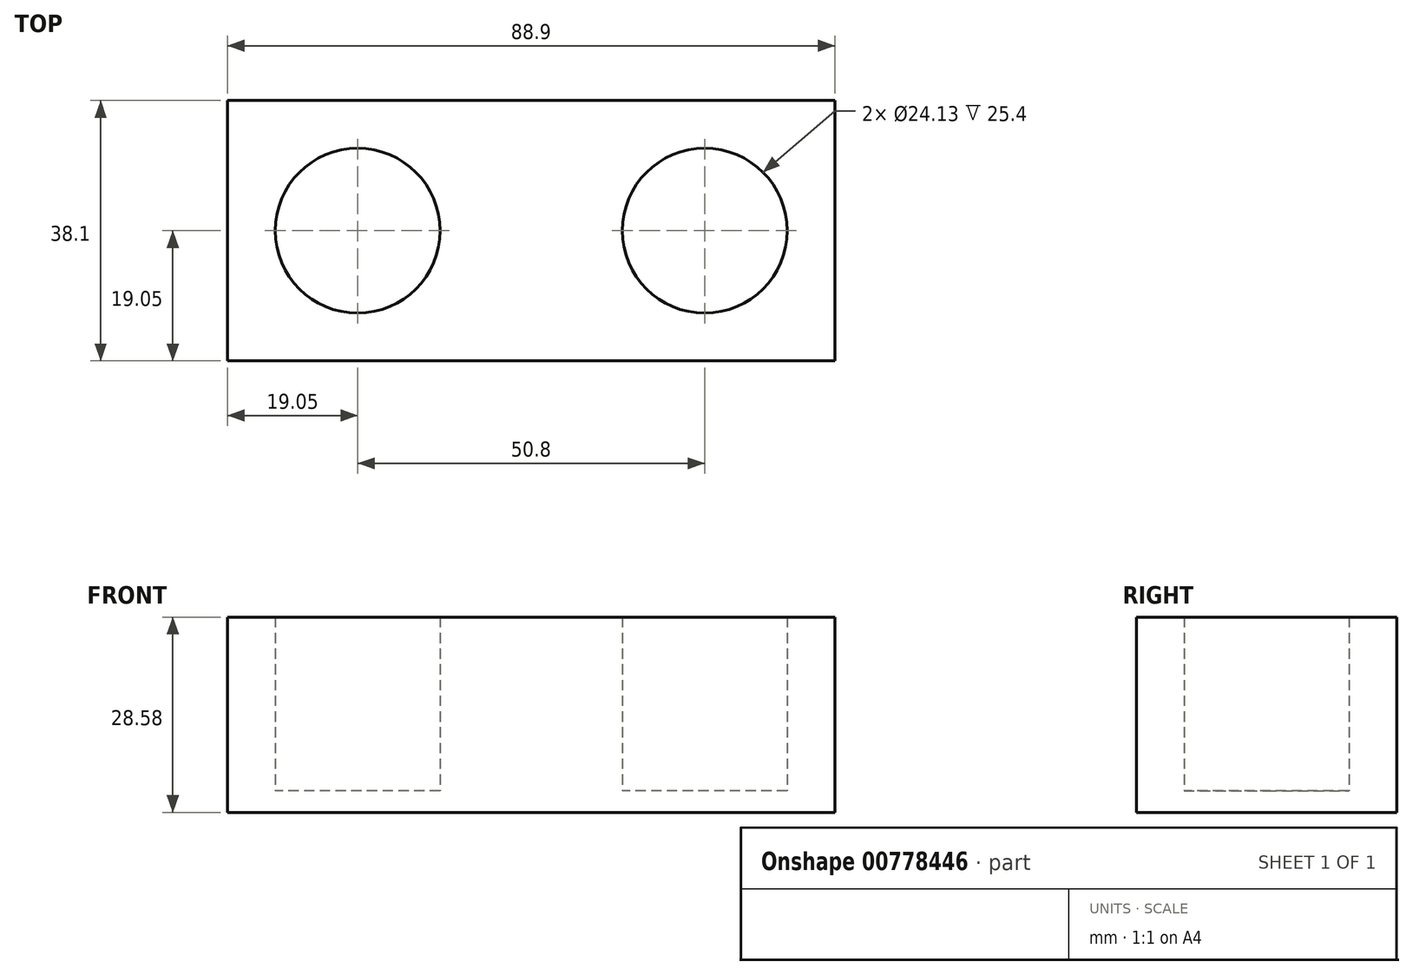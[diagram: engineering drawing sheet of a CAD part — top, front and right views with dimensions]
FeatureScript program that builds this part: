
annotation { "Feature Type Name" : "Feature", "Feature Type Description" : "" }
export const myFeature = defineFeature(function(context is Context, id is Id, definition is map)
    precondition{}
    {
        {
            var Q0;
            Q0=qCreatedBy(makeId("Top.planeOp"),FACE);
            var sketch = newSketch(context, id + "F0", { "sketchPlane" : qUnion([Q0])});
            skLineSegment(sketch, "E0.bottom", {"start": v(0, 0) * mm, "end": v(88.9, 0) * mm});
            skLineSegment(sketch, "E0.top", {"start": v(0, 38.1) * mm, "end": v(88.9, 38.1) * mm});
            skLineSegment(sketch, "E0.left", {"start": v(0, 0) * mm, "end": v(0, 38.1) * mm});
            skLineSegment(sketch, "E0.right", {"start": v(88.9, 0) * mm, "end": v(88.9, 38.1) * mm});
            skLineSegment(sketch, "E1", {"start": v(0, 38.1) * mm, "end": v(88.9, 0) * mm, "construction": true});
            skLineSegment(sketch, "E2", {"start": v(0, 19.05) * mm, "end": v(88.9, 19.05) * mm, "construction": true});
            skCircle(sketch, "E3", {"center": v(19.05, 19.05) * mm, "radius": 12.07 * mm});
            skCircle(sketch, "E4", {"center": v(69.85, 19.05) * mm, "radius": 12.07 * mm});
            skPoint(sketch, "E5", {"position": v(44.45, 19.05) * mm});
            skSolve(sketch);
        }
        {
            var Q0;
            Q0=makeQuery(id+"F0.imprint","IMPRINT",FACE,{"disambiguationData":[TD([[makeQuery(id+"F0.imprint","IMPRINT",EDGE,{"derivedFrom":sQuery(id+"F0.wireOp",EDGE,"E0.bottom")}),1.0]])]});
            extrude(context, id + "F1", {"entities" : qUnion([Q0]), "depth" : 25.4 * mm, "offsetDistance" : 25.4 * mm});
        }
        {
            var Q0;
            Q0=makeQuery(id+"F1.opExtrude","CAP_FACE",FACE,{"disambiguationData":[OSD([sQuery(id+"F0.wireOp",EDGE,"E0.bottom"),sQuery(id+"F0.wireOp",EDGE,"E0.top"),sQuery(id+"F0.wireOp",EDGE,"E0.left"),sQuery(id+"F0.wireOp",EDGE,"E0.right"),sQuery(id+"F0.wireOp",EDGE,"E3"),sQuery(id+"F0.wireOp",EDGE,"E4")])],"isStart":true});
            var sketch = newSketch(context, id + "F2", { "sketchPlane" : qUnion([Q0])});
            skLineSegment(sketch, "E6.bottom", {"start": v(0, -38.1) * mm, "end": v(88.9, -38.1) * mm});
            skLineSegment(sketch, "E6.top", {"start": v(0, 0) * mm, "end": v(88.9, 0) * mm});
            skLineSegment(sketch, "E6.left", {"start": v(0, -38.1) * mm, "end": v(0, 0) * mm});
            skLineSegment(sketch, "E6.right", {"start": v(88.9, -38.1) * mm, "end": v(88.9, 0) * mm});
            skSolve(sketch);
        }
        {
            var Q0;
            Q0 = qSketchRegion(id + "F2", true);
            extrude(context, id + "F3", {"entities" : qUnion([Q0]), "operationType" : NewBodyOperationType.ADD, "depth" : 3.17 * mm, "offsetDistance" : 25.4 * mm});
        }
    });
